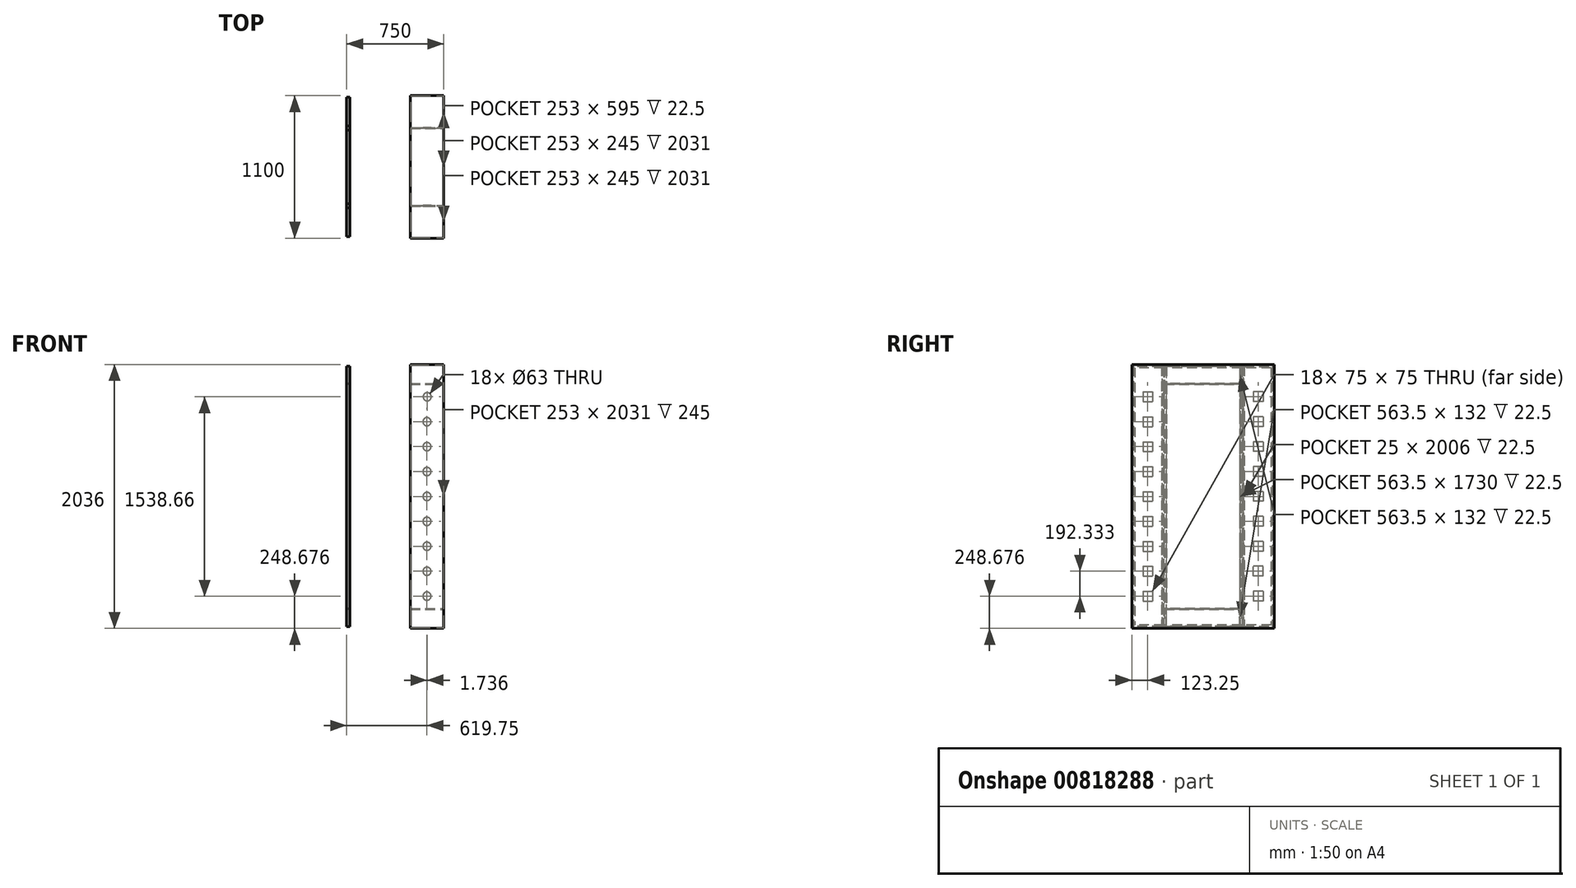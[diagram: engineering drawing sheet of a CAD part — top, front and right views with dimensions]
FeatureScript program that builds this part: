
annotation { "Feature Type Name" : "Feature", "Feature Type Description" : "" }
export const myFeature = defineFeature(function(context is Context, id is Id, definition is map)
    precondition{}
    {
        {
            var Q0;
            Q0=qCreatedBy(makeId("Right.planeOp"),FACE);
            var sketch = newSketch(context, id + "F0", { "sketchPlane" : qUnion([Q0])});
            skLineSegment(sketch, "E0.bottom", {"start": v(550, 1018) * mm, "end": v(-550, 1018) * mm});
            skLineSegment(sketch, "E0.top", {"start": v(550, -1018) * mm, "end": v(-550, -1018) * mm});
            skLineSegment(sketch, "E0.left", {"start": v(550, 1018) * mm, "end": v(550, -1018) * mm});
            skLineSegment(sketch, "E0.right", {"start": v(-550, 1018) * mm, "end": v(-550, -1018) * mm});
            skPoint(sketch, "E0.middle", {"position": v(0, 0) * mm});
            skSolve(sketch);
        }
        {
            var Q0;
            Q0 = qSketchRegion(id + "F0", true);
            extrude(context, id + "F1", {"entities" : qUnion([Q0]), "oppositeDirection" : true, "depth" : 258 * mm, "offsetDistance" : 25 * mm});
        }
        {
            var Q0;
            Q0=makeQuery(id+"F1.opExtrude","CAP_FACE",FACE,{"disambiguationData":[OSD([sQuery(id+"F0.wireOp",EDGE,"E0.bottom"),sQuery(id+"F0.wireOp",EDGE,"E0.top"),sQuery(id+"F0.wireOp",EDGE,"E0.left"),sQuery(id+"F0.wireOp",EDGE,"E0.right")])],"isStart":false});
            shell(context, id + "F2", {"entities" : qUnion([Q0]), "thickness" : 2.5 * mm});
        }
        {
            var Q0;
            Q0=makeQuery(id+"F1.opExtrude","CAP_FACE",FACE,{"disambiguationData":[OSD([sQuery(id+"F0.wireOp",EDGE,"E0.bottom"),sQuery(id+"F0.wireOp",EDGE,"E0.top"),sQuery(id+"F0.wireOp",EDGE,"E0.left"),sQuery(id+"F0.wireOp",EDGE,"E0.right")])],"isStart":true});
            var sketch = newSketch(context, id + "F3", { "sketchPlane" : qUnion([Q0])});
            skLineSegment(sketch, "E1.0", {"start": v(550, 1018) * mm, "end": v(-550, 1018) * mm, "construction": true});
            skLineSegment(sketch, "E2", {"start": v(-302.5, 1018) * mm, "end": v(-302.5, -1018) * mm});
            skLineSegment(sketch, "E3", {"start": v(302.5, 1018) * mm, "end": v(302.5, -1018) * mm});
            skLineSegment(sketch, "E4.0", {"start": v(-297.5, 1018) * mm, "end": v(-297.5, -1018) * mm});
            skLineSegment(sketch, "E5.0", {"start": v(297.5, 1018) * mm, "end": v(297.5, -1018) * mm});
            skLineSegment(sketch, "E6", {"start": v(-302.5, 1018) * mm, "end": v(-297.5, 1018) * mm});
            skLineSegment(sketch, "E7", {"start": v(297.5, 1018) * mm, "end": v(302.5, 1018) * mm});
            skLineSegment(sketch, "E8", {"start": v(297.5, -1018) * mm, "end": v(302.5, -1018) * mm});
            skLineSegment(sketch, "E9", {"start": v(-302.5, -1018) * mm, "end": v(-297.5, -1018) * mm});
            skLineSegment(sketch, "E10", {"start": v(-302.5, 870.5) * mm, "end": v(302.5, 870.5) * mm});
            skLineSegment(sketch, "E11", {"start": v(-302.5, -870.5) * mm, "end": v(302.5, -870.5) * mm});
            skLineSegment(sketch, "E12.0", {"start": v(-302.5, -865.5) * mm, "end": v(302.5, -865.5) * mm});
            skLineSegment(sketch, "E13.0", {"start": v(-302.5, 865.5) * mm, "end": v(302.5, 865.5) * mm});
            skSolve(sketch);
        }
        {
            var Q0;
            Q0 = qSketchRegion(id + "F3", true);
            extrude(context, id + "F4", {"entities" : qUnion([Q0]), "operationType" : NewBodyOperationType.ADD, "oppositeDirection" : true, "depth" : 258 * mm, "offsetDistance" : 25 * mm});
        }
        {
            var Q0;
            Q0=makeQuery(id+"F4.boolean.opBoolean","MERGE",FACE,{"derivedFrom":[makeQuery(id+"F1.opExtrude","CAP_FACE",FACE,{"disambiguationData":[OSD([sQuery(id+"F0.wireOp",EDGE,"E0.bottom"),sQuery(id+"F0.wireOp",EDGE,"E0.top"),sQuery(id+"F0.wireOp",EDGE,"E0.left"),sQuery(id+"F0.wireOp",EDGE,"E0.right")])],"isStart":false}),makeQuery(id+"F4.opExtrude","CAP_FACE",FACE,{"disambiguationData":[OSD([sQuery(id+"F3.wireOp",EDGE,"E2"),sQuery(id+"F3.wireOp",EDGE,"E3"),sQuery(id+"F3.wireOp",EDGE,"E4.0"),sQuery(id+"F3.wireOp",EDGE,"E5.0"),sQuery(id+"F3.wireOp",EDGE,"E6"),sQuery(id+"F3.wireOp",EDGE,"E7"),sQuery(id+"F3.wireOp",EDGE,"E8"),sQuery(id+"F3.wireOp",EDGE,"E9"),sQuery(id+"F3.wireOp",EDGE,"E10"),sQuery(id+"F3.wireOp",EDGE,"E11"),sQuery(id+"F3.wireOp",EDGE,"E12.0"),sQuery(id+"F3.wireOp",EDGE,"E13.0")])],"isStart":false})]});
            var sketch = newSketch(context, id + "F5", { "sketchPlane" : qUnion([Q0])});
            skLineSegment(sketch, "E14.0", {"start": v(-550, 1018) * mm, "end": v(550, 1018) * mm});
            skLineSegment(sketch, "E15.0", {"start": v(-550, 1018) * mm, "end": v(-550, -1018) * mm});
            skLineSegment(sketch, "E16.0", {"start": v(-550, -1018) * mm, "end": v(550, -1018) * mm});
            skLineSegment(sketch, "E17.0", {"start": v(550, 1018) * mm, "end": v(550, -1018) * mm});
            skLineSegment(sketch, "E18.0", {"start": v(-525, 993) * mm, "end": v(525, 993) * mm});
            skLineSegment(sketch, "E18.1", {"start": v(-525, 993) * mm, "end": v(-525, -993) * mm});
            skLineSegment(sketch, "E18.2", {"start": v(-525, -993) * mm, "end": v(525, -993) * mm});
            skLineSegment(sketch, "E18.3", {"start": v(525, 993) * mm, "end": v(525, -993) * mm});
            skSolve(sketch);
        }
        {
            var Q0;
            Q0 = qSketchRegion(id + "F5", true);
            extrude(context, id + "F6", {"entities" : qUnion([Q0]), "operationType" : NewBodyOperationType.ADD, "oppositeDirection" : true, "depth" : 2.5 * mm, "offsetDistance" : 25 * mm});
        }
        {
            var Q0;
            Q0=makeQuery(id+"F4.opExtrude","SWEPT_FACE",FACE,{"disambiguationData":[OSD([sQuery(id+"F3.wireOp",EDGE,"E3")])]});
            var sketch = newSketch(context, id + "F7", { "sketchPlane" : qUnion([Q0])});
            skPoint(sketch, "E19.0", {"position": v(258, 865.5) * mm});
            skPoint(sketch, "E20.0", {"position": v(258, -865.5) * mm});
            skLineSegment(sketch, "E21.0", {"start": v(2.5, 1015.5) * mm, "end": v(2.5, -1015.5) * mm, "construction": true});
            skLineSegment(sketch, "E22", {"start": v(258, -865.5) * mm, "end": v(2.5, -865.5) * mm, "construction": true});
            skLineSegment(sketch, "E23", {"start": v(258, 865.5) * mm, "end": v(2.5, 865.5) * mm, "construction": true});
            skCircle(sketch, "E24", {"center": v(128.51, 769.34) * mm, "radius": 31.5 * mm});
            skCircle(sketch, "E25", {"center": v(130.25, 577) * mm, "radius": 31.5 * mm});
            skCircle(sketch, "E26", {"center": v(130.25, 384.67) * mm, "radius": 31.5 * mm});
            skCircle(sketch, "E27", {"center": v(130.25, 192.34) * mm, "radius": 31.5 * mm});
            skCircle(sketch, "E28", {"center": v(130.25, 0) * mm, "radius": 31.5 * mm});
            skCircle(sketch, "E29", {"center": v(130.25, -192.33) * mm, "radius": 31.5 * mm});
            skCircle(sketch, "E30", {"center": v(130.25, -384.66) * mm, "radius": 31.5 * mm});
            skCircle(sketch, "E31", {"center": v(130.25, -577) * mm, "radius": 31.5 * mm});
            skCircle(sketch, "E32", {"center": v(130.25, -769.32) * mm, "radius": 31.5 * mm});
            skLineSegment(sketch, "E33", {"start": v(128.51, 769.34) * mm, "end": v(130.25, 865.5) * mm, "construction": true});
            skLineSegment(sketch, "E34", {"start": v(130.25, -769.32) * mm, "end": v(130.25, -865.5) * mm, "construction": true});
            skSolve(sketch);
        }
        {
            var Q0;
            Q0 = qSketchRegion(id + "F7", true);
            extrude(context, id + "F8", {"entities" : qUnion([Q0]), "operationType" : NewBodyOperationType.REMOVE, "oppositeDirection" : true, "depth" : 706 * mm, "offsetDistance" : 25 * mm});
        }
        {
            var Q0;
            Q0=qCreatedBy(makeId("Right.planeOp"),FACE);
            cPlane(context, id + "F9", {"entities" : qUnion([Q0]), "cplaneType" : CPlaneType.OFFSET, "offset" : 750 * mm, "oppositeDirection" : true, "width" : 150 * mm, "height" : 150 * mm});
        }
        {
            var Q0;
            Q0=qCreatedBy(id+"F9.planeOp",FACE);
            var sketch = newSketch(context, id + "F10", { "sketchPlane" : qUnion([Q0])});
            skPoint(sketch, "E35.0", {"position": v(302.5, 993) * mm});
            skPoint(sketch, "E36.0", {"position": v(297.5, 993) * mm});
            skPoint(sketch, "E37.0", {"position": v(-297.5, 993) * mm});
            skPoint(sketch, "E38.0", {"position": v(-302.5, 993) * mm});
            skLineSegment(sketch, "E39", {"start": v(302.5, 993) * mm, "end": v(297.5, 993) * mm, "construction": true});
            skLineSegment(sketch, "E40", {"start": v(285.5, 1005.5) * mm, "end": v(285.5, -1005.5) * mm});
            skLineSegment(sketch, "E41", {"start": v(315.5, -1005.5) * mm, "end": v(315.5, 1005.5) * mm});
            skLineSegment(sketch, "E42", {"start": v(-297.5, 993) * mm, "end": v(-302.5, 993) * mm, "construction": true});
            skPoint(sketch, "E43.orphan", {"position": v(285.5, 993) * mm});
            skLineSegment(sketch, "E44", {"start": v(-300, 993) * mm, "end": v(-300, 1005.5) * mm, "construction": true});
            skLineSegment(sketch, "E45", {"start": v(-300, 1005.5) * mm, "end": v(-285, 1005.5) * mm});
            skLineSegment(sketch, "E46", {"start": v(-285, 1005.5) * mm, "end": v(-285, -1005.5) * mm});
            skLineSegment(sketch, "E47", {"start": v(-315, -1005.5) * mm, "end": v(-315, 1005.5) * mm});
            skLineSegment(sketch, "E48", {"start": v(-315, 1005.5) * mm, "end": v(-285, 1005.5) * mm});
            skLineSegment(sketch, "E49", {"start": v(297.5, 865.5) * mm, "end": v(297.5, 870.5) * mm, "construction": true});
            skLineSegment(sketch, "E50", {"start": v(297.5, 868) * mm, "end": v(-333.18, 868) * mm, "construction": true});
            skLineSegment(sketch, "E51.bottom", {"start": v(284.5, 1005.5) * mm, "end": v(-284, 1005.5) * mm});
            skLineSegment(sketch, "E51.top", {"start": v(284.5, 868.5) * mm, "end": v(-284, 868.5) * mm});
            skLineSegment(sketch, "E51.left", {"start": v(284.5, 1005.5) * mm, "end": v(284.5, 868.5) * mm});
            skLineSegment(sketch, "E51.right", {"start": v(-284, 1005.5) * mm, "end": v(-284, 868.5) * mm});
            skLineSegment(sketch, "E52", {"start": v(315.5, 0) * mm, "end": v(-315, 0) * mm, "construction": true});
            skLineSegment(sketch, "E53.MirrorCS", {"start": v(284.5, -1005.5) * mm, "end": v(284.5, -868.5) * mm});
            skLineSegment(sketch, "E54.MirrorCS", {"start": v(284.5, -868.5) * mm, "end": v(-284, -868.5) * mm});
            skLineSegment(sketch, "E55.MirrorCS", {"start": v(-284, -1005.5) * mm, "end": v(-284, -868.5) * mm});
            skLineSegment(sketch, "E56", {"start": v(284.5, -1005.5) * mm, "end": v(-284, -1005.5) * mm});
            skLineSegment(sketch, "E57.0", {"start": v(525, 993) * mm, "end": v(302.5, 993) * mm, "construction": true});
            skLineSegment(sketch, "E58", {"start": v(285.5, 1005.5) * mm, "end": v(315.5, 1005.5) * mm});
            skPoint(sketch, "E59.orphan", {"position": v(285.5, 1018) * mm});
            skPoint(sketch, "E60.orphan", {"position": v(315.5, 1018) * mm});
            skLineSegment(sketch, "E61", {"start": v(285.5, -1005.5) * mm, "end": v(315.5, -1005.5) * mm});
            skPoint(sketch, "E62.start.orphan", {"position": v(285.5, -1018) * mm});
            skPoint(sketch, "E63.orphan", {"position": v(315.5, -1018) * mm});
            skLineSegment(sketch, "E64", {"start": v(-285, -1005.5) * mm, "end": v(-315, -1005.5) * mm});
            skLineSegment(sketch, "E65.bottom", {"start": v(284.5, 867.5) * mm, "end": v(-284, 867.5) * mm});
            skLineSegment(sketch, "E65.top", {"start": v(284.5, -867.5) * mm, "end": v(-284, -867.5) * mm});
            skLineSegment(sketch, "E65.left", {"start": v(284.5, 867.5) * mm, "end": v(284.5, -867.5) * mm});
            skLineSegment(sketch, "E65.right", {"start": v(-284, 867.5) * mm, "end": v(-284, -867.5) * mm});
            skLineSegment(sketch, "E66.0", {"start": v(550, 1018) * mm, "end": v(550, -1018) * mm, "construction": true});
            skLineSegment(sketch, "E67.bottom", {"start": v(316.5, 1005.5) * mm, "end": v(537.5, 1005.5) * mm});
            skLineSegment(sketch, "E67.top", {"start": v(316.5, -1005.5) * mm, "end": v(537.5, -1005.5) * mm});
            skLineSegment(sketch, "E67.left", {"start": v(316.5, 1005.5) * mm, "end": v(316.5, -1005.5) * mm});
            skLineSegment(sketch, "E67.right", {"start": v(537.5, 1005.5) * mm, "end": v(537.5, -1005.5) * mm});
            skLineSegment(sketch, "E68.bottom", {"start": v(-316, 1005.5) * mm, "end": v(-537.5, 1005.5) * mm});
            skLineSegment(sketch, "E68.top", {"start": v(-316, -1005.5) * mm, "end": v(-537.5, -1005.5) * mm});
            skLineSegment(sketch, "E68.left", {"start": v(-316, 1005.5) * mm, "end": v(-316, -1005.5) * mm});
            skLineSegment(sketch, "E68.right", {"start": v(-537.5, 1005.5) * mm, "end": v(-537.5, -1005.5) * mm});
            skSolve(sketch);
        }
        {
            var Q0;
            Q0 = qSketchRegion(id + "F10", true);
            extrude(context, id + "F11", {"entities" : qUnion([Q0]), "depth" : 25 * mm, "offsetDistance" : 25 * mm});
        }
        {
            var Q0;
            Q0=makeQuery(id+"F11.opExtrude","CAP_FACE",FACE,{"disambiguationData":[OSD([sQuery(id+"F10.wireOp",EDGE,"dcfa3433-e3b1-478e-ab3f-8db6d5a730070.MirrorCS"),sQuery(id+"F10.wireOp",EDGE,"3de99439-b079-4a28-83e3-573c53d0b4500.MirrorCS"),sQuery(id+"F10.wireOp",EDGE,"6f84274e-3925-4807-9f6e-ac1c9427b1030.MirrorCS"),sQuery(id+"F10.wireOp",EDGE,"n2yFbVMf-GZ9d-6t0V-9odt-Dh0pJaJmG94E")])],"isStart":false});
            var Q1;
            Q1=makeQuery(id+"F11.opExtrude","CAP_FACE",FACE,{"disambiguationData":[OSD([sQuery(id+"F10.wireOp",EDGE,"iE6rTO2U-B8h5-sTnw-McQn-db4rVg8K6M3c"),sQuery(id+"F10.wireOp",EDGE,"E40"),sQuery(id+"F10.wireOp",EDGE,"E62"),sQuery(id+"F10.wireOp",EDGE,"E41")])],"isStart":false});
            shell(context, id + "F12", {"entities" : qUnion([Q0, Q1]), "thickness" : 2.5 * mm});
        }
        {
            var Q0;
            Q0=makeQuery(id+"F11.opExtrude","CAP_FACE",FACE,{"disambiguationData":[OSD([sQuery(id+"F10.wireOp",EDGE,"E67.bottom"),sQuery(id+"F10.wireOp",EDGE,"E67.top"),sQuery(id+"F10.wireOp",EDGE,"E67.left"),sQuery(id+"F10.wireOp",EDGE,"E67.right")])],"isStart":true});
            var sketch = newSketch(context, id + "F13", { "sketchPlane" : qUnion([Q0])});
            skLineSegment(sketch, "E69.0", {"start": v(-302.5, 737.84) * mm, "end": v(-302.5, 800.84) * mm, "construction": true});
            skLineSegment(sketch, "E70.0", {"start": v(-302.5, 545.5) * mm, "end": v(-302.5, 608.5) * mm, "construction": true});
            skLineSegment(sketch, "E71.0", {"start": v(-302.5, 353.17) * mm, "end": v(-302.5, 416.17) * mm, "construction": true});
            skLineSegment(sketch, "E72.0", {"start": v(-302.5, 160.84) * mm, "end": v(-302.5, 223.84) * mm, "construction": true});
            skLineSegment(sketch, "E73.0", {"start": v(-297.5, 31.5) * mm, "end": v(-297.5, -31.5) * mm, "construction": true});
            skLineSegment(sketch, "E74.0", {"start": v(-302.5, -223.83) * mm, "end": v(-302.5, -160.83) * mm, "construction": true});
            skLineSegment(sketch, "E75.0", {"start": v(-302.5, -608.5) * mm, "end": v(-302.5, -545.5) * mm, "construction": true});
            skLineSegment(sketch, "E76.0", {"start": v(-302.5, -800.82) * mm, "end": v(-302.5, -737.82) * mm, "construction": true});
            skLineSegment(sketch, "E77.0", {"start": v(-302.5, -416.16) * mm, "end": v(-302.5, -353.16) * mm, "construction": true});
            skLineSegment(sketch, "E78.0", {"start": v(-316.5, 1005.5) * mm, "end": v(-537.5, 1005.5) * mm, "construction": true});
            skLineSegment(sketch, "E79", {"start": v(-427, 1005.5) * mm, "end": v(-427, -1005.5) * mm, "construction": true});
            skLineSegment(sketch, "E80.bottom", {"start": v(-464.5, -731.82) * mm, "end": v(-389.5, -731.82) * mm});
            skLineSegment(sketch, "E80.top", {"start": v(-464.5, -806.82) * mm, "end": v(-389.5, -806.82) * mm});
            skLineSegment(sketch, "E80.left", {"start": v(-464.5, -731.82) * mm, "end": v(-464.5, -806.82) * mm});
            skLineSegment(sketch, "E80.right", {"start": v(-389.5, -731.82) * mm, "end": v(-389.5, -806.82) * mm});
            skPoint(sketch, "E80.middle", {"position": v(-427, -769.32) * mm});
            skLineSegment(sketch, "E81", {"start": v(-302.5, -769.32) * mm, "end": v(-302.5, -769.32) * mm});
            skPoint(sketch, "E81.endSnap0", {"position": v(-302.5, -769.32) * mm});
            skLineSegment(sketch, "E82", {"start": v(-302.5, -769.32) * mm, "end": v(-508.33, -769.32) * mm, "construction": true});
            skLineSegment(sketch, "E83", {"start": v(-302.5, 769.34) * mm, "end": v(-427, 769.34) * mm, "construction": true});
            skLineSegment(sketch, "E84", {"start": v(-302.5, 577) * mm, "end": v(-427, 577) * mm, "construction": true});
            skLineSegment(sketch, "E85", {"start": v(-302.5, 384.67) * mm, "end": v(-427, 384.67) * mm, "construction": true});
            skLineSegment(sketch, "E86", {"start": v(-302.5, 192.34) * mm, "end": v(-427, 192.34) * mm, "construction": true});
            skLineSegment(sketch, "E87", {"start": v(-297.5, 0) * mm, "end": v(-427, 0) * mm, "construction": true});
            skPoint(sketch, "E87.endSnap0", {"position": v(-297.5, 0) * mm});
            skLineSegment(sketch, "E88", {"start": v(-302.5, -192.33) * mm, "end": v(-427, -192.33) * mm, "construction": true});
            skLineSegment(sketch, "E89", {"start": v(-302.5, -384.66) * mm, "end": v(-427, -384.66) * mm, "construction": true});
            skLineSegment(sketch, "E90", {"start": v(-302.5, -577) * mm, "end": v(-427, -577) * mm, "construction": true});
            skLineSegment(sketch, "E91.bottom", {"start": v(-464.5, -614.5) * mm, "end": v(-389.5, -614.5) * mm});
            skLineSegment(sketch, "E91.top", {"start": v(-464.5, -539.5) * mm, "end": v(-389.5, -539.5) * mm});
            skLineSegment(sketch, "E91.left", {"start": v(-464.5, -614.5) * mm, "end": v(-464.5, -539.5) * mm});
            skLineSegment(sketch, "E91.right", {"start": v(-389.5, -614.5) * mm, "end": v(-389.5, -539.5) * mm});
            skPoint(sketch, "E91.middle", {"position": v(-427, -577) * mm});
            skLineSegment(sketch, "E92.bottom", {"start": v(-464.5, -347.16) * mm, "end": v(-389.5, -347.16) * mm});
            skLineSegment(sketch, "E92.top", {"start": v(-464.5, -422.16) * mm, "end": v(-389.5, -422.16) * mm});
            skLineSegment(sketch, "E92.left", {"start": v(-464.5, -347.16) * mm, "end": v(-464.5, -422.16) * mm});
            skLineSegment(sketch, "E92.right", {"start": v(-389.5, -347.16) * mm, "end": v(-389.5, -422.16) * mm});
            skPoint(sketch, "E92.middle", {"position": v(-427, -384.66) * mm});
            skLineSegment(sketch, "E93.bottom", {"start": v(-464.5, -154.83) * mm, "end": v(-389.5, -154.83) * mm});
            skLineSegment(sketch, "E93.top", {"start": v(-464.5, -229.83) * mm, "end": v(-389.5, -229.83) * mm});
            skLineSegment(sketch, "E93.left", {"start": v(-464.5, -154.83) * mm, "end": v(-464.5, -229.83) * mm});
            skLineSegment(sketch, "E93.right", {"start": v(-389.5, -154.83) * mm, "end": v(-389.5, -229.83) * mm});
            skPoint(sketch, "E93.middle", {"position": v(-427, -192.33) * mm});
            skLineSegment(sketch, "E94.bottom", {"start": v(-464.5, 37.5) * mm, "end": v(-389.5, 37.5) * mm});
            skLineSegment(sketch, "E94.top", {"start": v(-464.5, -37.5) * mm, "end": v(-389.5, -37.5) * mm});
            skLineSegment(sketch, "E94.left", {"start": v(-464.5, 37.5) * mm, "end": v(-464.5, -37.5) * mm});
            skLineSegment(sketch, "E94.right", {"start": v(-389.5, 37.5) * mm, "end": v(-389.5, -37.5) * mm});
            skPoint(sketch, "E94.middle", {"position": v(-427, 0) * mm});
            skLineSegment(sketch, "E95.bottom", {"start": v(-464.5, 229.84) * mm, "end": v(-389.5, 229.84) * mm});
            skLineSegment(sketch, "E95.top", {"start": v(-464.5, 154.84) * mm, "end": v(-389.5, 154.84) * mm});
            skLineSegment(sketch, "E95.left", {"start": v(-464.5, 229.84) * mm, "end": v(-464.5, 154.84) * mm});
            skLineSegment(sketch, "E95.right", {"start": v(-389.5, 229.84) * mm, "end": v(-389.5, 154.84) * mm});
            skPoint(sketch, "E95.middle", {"position": v(-427, 192.34) * mm});
            skLineSegment(sketch, "E96.bottom", {"start": v(-464.5, 422.17) * mm, "end": v(-389.5, 422.17) * mm});
            skLineSegment(sketch, "E96.top", {"start": v(-464.5, 347.17) * mm, "end": v(-389.5, 347.17) * mm});
            skLineSegment(sketch, "E96.left", {"start": v(-464.5, 422.17) * mm, "end": v(-464.5, 347.17) * mm});
            skLineSegment(sketch, "E96.right", {"start": v(-389.5, 422.17) * mm, "end": v(-389.5, 347.17) * mm});
            skPoint(sketch, "E96.middle", {"position": v(-427, 384.67) * mm});
            skLineSegment(sketch, "E97.bottom", {"start": v(-464.5, 614.5) * mm, "end": v(-389.5, 614.5) * mm});
            skLineSegment(sketch, "E97.top", {"start": v(-464.5, 539.5) * mm, "end": v(-389.5, 539.5) * mm});
            skLineSegment(sketch, "E97.left", {"start": v(-464.5, 614.5) * mm, "end": v(-464.5, 539.5) * mm});
            skLineSegment(sketch, "E97.right", {"start": v(-389.5, 614.5) * mm, "end": v(-389.5, 539.5) * mm});
            skPoint(sketch, "E97.middle", {"position": v(-427, 577) * mm});
            skLineSegment(sketch, "E98.bottom", {"start": v(-464.5, 806.84) * mm, "end": v(-389.5, 806.84) * mm});
            skLineSegment(sketch, "E98.top", {"start": v(-464.5, 731.84) * mm, "end": v(-389.5, 731.84) * mm});
            skLineSegment(sketch, "E98.left", {"start": v(-464.5, 806.84) * mm, "end": v(-464.5, 731.84) * mm});
            skLineSegment(sketch, "E98.right", {"start": v(-389.5, 806.84) * mm, "end": v(-389.5, 731.84) * mm});
            skPoint(sketch, "E98.middle", {"position": v(-427, 769.34) * mm});
            skLineSegment(sketch, "E99", {"start": v(0, 848.75) * mm, "end": v(0, 224.46) * mm, "construction": true});
            skSolve(sketch);
        }
        {
            var Q0;
            Q0=makeQuery(id+"F11.opExtrude","CAP_FACE",FACE,{"disambiguationData":[OSD([sQuery(id+"F10.wireOp",EDGE,"E68.bottom"),sQuery(id+"F10.wireOp",EDGE,"E68.top"),sQuery(id+"F10.wireOp",EDGE,"E68.left"),sQuery(id+"F10.wireOp",EDGE,"E68.right")])],"isStart":true});
            var sketch = newSketch(context, id + "F14", { "sketchPlane" : qUnion([Q0])});
            skLineSegment(sketch, "E100.0", {"start": v(-389.5, 806.84) * mm, "end": v(-464.5, 806.84) * mm, "construction": true});
            skLineSegment(sketch, "E101.0", {"start": v(-389.5, 614.5) * mm, "end": v(-464.5, 614.5) * mm, "construction": true});
            skLineSegment(sketch, "E102.0", {"start": v(-389.5, 422.17) * mm, "end": v(-464.5, 422.17) * mm, "construction": true});
            skLineSegment(sketch, "E103.0", {"start": v(-464.5, 229.84) * mm, "end": v(-389.5, 229.84) * mm, "construction": true});
            skLineSegment(sketch, "E104.0", {"start": v(-464.5, 37.5) * mm, "end": v(-389.5, 37.5) * mm, "construction": true});
            skLineSegment(sketch, "E105.0", {"start": v(-464.5, -154.83) * mm, "end": v(-389.5, -154.83) * mm, "construction": true});
            skLineSegment(sketch, "E106.0", {"start": v(-464.5, -347.16) * mm, "end": v(-389.5, -347.16) * mm, "construction": true});
            skLineSegment(sketch, "E107.0", {"start": v(-464.5, -539.5) * mm, "end": v(-389.5, -539.5) * mm, "construction": true});
            skLineSegment(sketch, "E108.0", {"start": v(-464.5, -731.82) * mm, "end": v(-389.5, -731.82) * mm, "construction": true});
            skLineSegment(sketch, "E109", {"start": v(-389.5, -731.82) * mm, "end": v(493.15, -731.82) * mm, "construction": true});
            skLineSegment(sketch, "E110", {"start": v(-389.5, -539.5) * mm, "end": v(493.15, -539.5) * mm, "construction": true});
            skLineSegment(sketch, "E111", {"start": v(-389.5, -347.16) * mm, "end": v(493.15, -347.16) * mm, "construction": true});
            skLineSegment(sketch, "E112", {"start": v(-389.5, -154.83) * mm, "end": v(493.15, -154.83) * mm, "construction": true});
            skLineSegment(sketch, "E113", {"start": v(-389.5, 37.5) * mm, "end": v(493.15, 37.5) * mm, "construction": true});
            skLineSegment(sketch, "E114", {"start": v(-389.5, 229.84) * mm, "end": v(493.15, 229.84) * mm, "construction": true});
            skLineSegment(sketch, "E115", {"start": v(-389.5, 422.17) * mm, "end": v(493.15, 422.17) * mm, "construction": true});
            skLineSegment(sketch, "E116", {"start": v(-389.5, 614.5) * mm, "end": v(493.15, 614.5) * mm, "construction": true});
            skLineSegment(sketch, "E117", {"start": v(-389.5, 806.84) * mm, "end": v(493.15, 806.84) * mm, "construction": true});
            skLineSegment(sketch, "E118.0", {"start": v(316, 1005.5) * mm, "end": v(537.5, 1005.5) * mm, "construction": true});
            skLineSegment(sketch, "E119", {"start": v(426.75, 1005.5) * mm, "end": v(426.75, -1005.5) * mm, "construction": true});
            skLineSegment(sketch, "E120.bottom", {"start": v(464.25, -731.82) * mm, "end": v(389.25, -731.82) * mm});
            skLineSegment(sketch, "E120.top", {"start": v(464.25, -806.82) * mm, "end": v(389.25, -806.82) * mm});
            skLineSegment(sketch, "E120.left", {"start": v(464.25, -731.82) * mm, "end": v(464.25, -806.82) * mm});
            skLineSegment(sketch, "E120.right", {"start": v(389.25, -731.82) * mm, "end": v(389.25, -806.82) * mm});
            skLineSegment(sketch, "E121.bottom", {"start": v(464.25, -539.5) * mm, "end": v(389.25, -539.5) * mm});
            skLineSegment(sketch, "E121.top", {"start": v(464.25, -614.5) * mm, "end": v(389.25, -614.5) * mm});
            skLineSegment(sketch, "E121.left", {"start": v(464.25, -539.5) * mm, "end": v(464.25, -614.5) * mm});
            skLineSegment(sketch, "E121.right", {"start": v(389.25, -539.5) * mm, "end": v(389.25, -614.5) * mm});
            skLineSegment(sketch, "E122.bottom", {"start": v(464.25, -347.16) * mm, "end": v(389.25, -347.16) * mm});
            skLineSegment(sketch, "E122.top", {"start": v(464.25, -422.16) * mm, "end": v(389.25, -422.16) * mm});
            skLineSegment(sketch, "E122.left", {"start": v(464.25, -347.16) * mm, "end": v(464.25, -422.16) * mm});
            skLineSegment(sketch, "E122.right", {"start": v(389.25, -347.16) * mm, "end": v(389.25, -422.16) * mm});
            skLineSegment(sketch, "E123.bottom", {"start": v(464.25, -154.83) * mm, "end": v(389.25, -154.83) * mm});
            skLineSegment(sketch, "E123.top", {"start": v(464.25, -229.83) * mm, "end": v(389.25, -229.83) * mm});
            skLineSegment(sketch, "E123.left", {"start": v(464.25, -154.83) * mm, "end": v(464.25, -229.83) * mm});
            skLineSegment(sketch, "E123.right", {"start": v(389.25, -154.83) * mm, "end": v(389.25, -229.83) * mm});
            skLineSegment(sketch, "E124.bottom", {"start": v(464.25, 37.5) * mm, "end": v(389.25, 37.5) * mm});
            skLineSegment(sketch, "E124.top", {"start": v(464.25, -37.5) * mm, "end": v(389.25, -37.5) * mm});
            skLineSegment(sketch, "E124.left", {"start": v(464.25, 37.5) * mm, "end": v(464.25, -37.5) * mm});
            skLineSegment(sketch, "E124.right", {"start": v(389.25, 37.5) * mm, "end": v(389.25, -37.5) * mm});
            skLineSegment(sketch, "E125.bottom", {"start": v(464.25, 229.84) * mm, "end": v(389.25, 229.84) * mm});
            skLineSegment(sketch, "E125.top", {"start": v(464.25, 154.84) * mm, "end": v(389.25, 154.84) * mm});
            skLineSegment(sketch, "E125.left", {"start": v(464.25, 229.84) * mm, "end": v(464.25, 154.84) * mm});
            skLineSegment(sketch, "E125.right", {"start": v(389.25, 229.84) * mm, "end": v(389.25, 154.84) * mm});
            skLineSegment(sketch, "E126.bottom", {"start": v(464.25, 614.5) * mm, "end": v(389.25, 614.5) * mm});
            skLineSegment(sketch, "E126.top", {"start": v(464.25, 539.5) * mm, "end": v(389.25, 539.5) * mm});
            skLineSegment(sketch, "E126.left", {"start": v(464.25, 614.5) * mm, "end": v(464.25, 539.5) * mm});
            skLineSegment(sketch, "E126.right", {"start": v(389.25, 614.5) * mm, "end": v(389.25, 539.5) * mm});
            skLineSegment(sketch, "E127.bottom", {"start": v(464.25, 806.84) * mm, "end": v(389.25, 806.84) * mm});
            skLineSegment(sketch, "E127.top", {"start": v(464.25, 731.84) * mm, "end": v(389.25, 731.84) * mm});
            skLineSegment(sketch, "E127.left", {"start": v(464.25, 806.84) * mm, "end": v(464.25, 731.84) * mm});
            skLineSegment(sketch, "E127.right", {"start": v(389.25, 806.84) * mm, "end": v(389.25, 731.84) * mm});
            skLineSegment(sketch, "E128.bottom", {"start": v(464.25, 422.17) * mm, "end": v(389.25, 422.17) * mm});
            skLineSegment(sketch, "E128.top", {"start": v(464.25, 347.17) * mm, "end": v(389.25, 347.17) * mm});
            skLineSegment(sketch, "E128.left", {"start": v(464.25, 422.17) * mm, "end": v(464.25, 347.17) * mm});
            skLineSegment(sketch, "E128.right", {"start": v(389.25, 422.17) * mm, "end": v(389.25, 347.17) * mm});
            skSolve(sketch);
        }
        {
            var Q0;
            Q0=makeQuery(id+"F11.opExtrude","CAP_FACE",FACE,{"disambiguationData":[OSD([sQuery(id+"F10.wireOp",EDGE,"E67.bottom"),sQuery(id+"F10.wireOp",EDGE,"E67.top"),sQuery(id+"F10.wireOp",EDGE,"E67.left"),sQuery(id+"F10.wireOp",EDGE,"E67.right")])],"isStart":false});
            var Q1;
            Q1=makeQuery(id+"F11.opExtrude","CAP_FACE",FACE,{"disambiguationData":[OSD([sQuery(id+"F10.wireOp",EDGE,"E68.bottom"),sQuery(id+"F10.wireOp",EDGE,"E68.top"),sQuery(id+"F10.wireOp",EDGE,"E68.left"),sQuery(id+"F10.wireOp",EDGE,"E68.right")])],"isStart":false});
            var Q2;
            Q2=makeQuery(id+"F11.opExtrude","CAP_FACE",FACE,{"disambiguationData":[OSD([sQuery(id+"F10.wireOp",EDGE,"E65.bottom"),sQuery(id+"F10.wireOp",EDGE,"E65.top"),sQuery(id+"F10.wireOp",EDGE,"E65.left"),sQuery(id+"F10.wireOp",EDGE,"E65.right")])],"isStart":false});
            var Q3;
            Q3=makeQuery(id+"F11.opExtrude","CAP_FACE",FACE,{"disambiguationData":[OSD([sQuery(id+"F10.wireOp",EDGE,"E51.bottom"),sQuery(id+"F10.wireOp",EDGE,"E51.top"),sQuery(id+"F10.wireOp",EDGE,"E51.left"),sQuery(id+"F10.wireOp",EDGE,"E51.right")])],"isStart":false});
            var Q4;
            Q4=makeQuery(id+"F11.opExtrude","CAP_FACE",FACE,{"disambiguationData":[OSD([sQuery(id+"F10.wireOp",EDGE,"E53.MirrorCS"),sQuery(id+"F10.wireOp",EDGE,"E54.MirrorCS"),sQuery(id+"F10.wireOp",EDGE,"E55.MirrorCS"),sQuery(id+"F10.wireOp",EDGE,"E56")])],"isStart":false});
            shell(context, id + "F15", {"entities" : qUnion([Q0, Q1, Q2, Q3, Q4]), "thickness" : 2.5 * mm});
        }
        {
            var Q0;
            Q0 = qSketchRegion(id + "F13", true);
            extrude(context, id + "F16", {"entities" : qUnion([Q0]), "operationType" : NewBodyOperationType.REMOVE, "oppositeDirection" : true, "depth" : 25 * mm, "offsetDistance" : 25 * mm});
        }
        {
            var Q0;
            Q0 = qSketchRegion(id + "F14", true);
            extrude(context, id + "F17", {"entities" : qUnion([Q0]), "operationType" : NewBodyOperationType.REMOVE, "oppositeDirection" : true, "depth" : 25 * mm, "offsetDistance" : 25 * mm});
        }
    });
